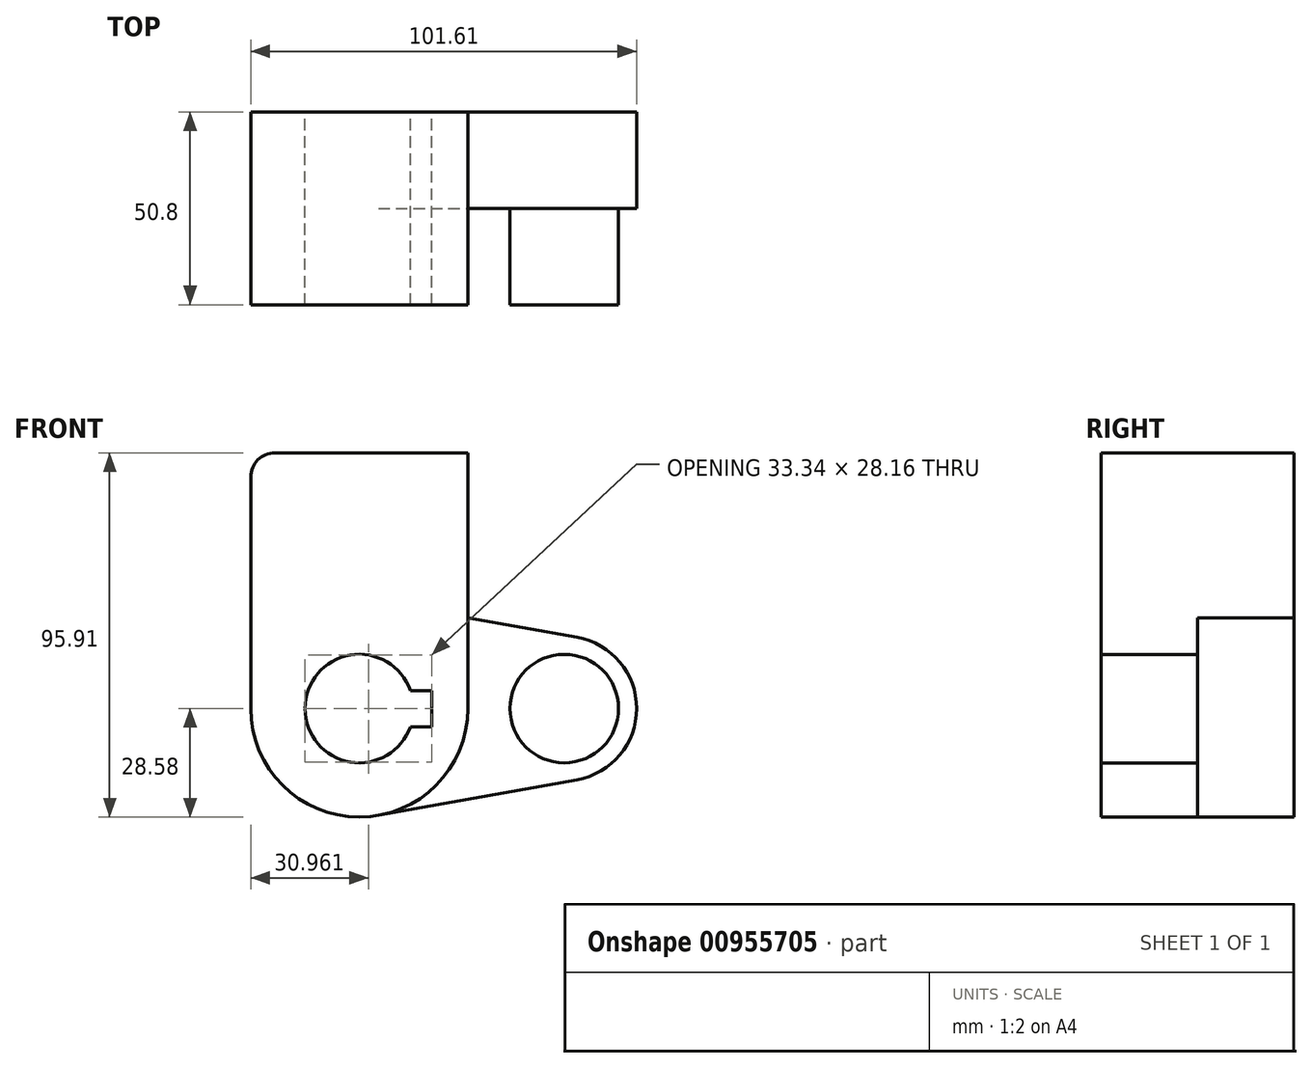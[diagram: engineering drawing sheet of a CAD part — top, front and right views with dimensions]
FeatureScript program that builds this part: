
annotation { "Feature Type Name" : "Feature", "Feature Type Description" : "" }
export const myFeature = defineFeature(function(context is Context, id is Id, definition is map)
    precondition{}
    {
        {
            var Q0;
            Q0=qCreatedBy(makeId("Front.planeOp"),FACE);
            var sketch = newSketch(context, id + "F0", { "sketchPlane" : qUnion([Q0])});
            skCircle(sketch, "E0", {"center": v(0, 0) * mm, "radius": 28.58 * mm});
            skCircle(sketch, "E1", {"center": v(53.98, 0) * mm, "radius": 19.05 * mm});
            skLineSegment(sketch, "E2", {"start": v(5.04, 28.13) * mm, "end": v(57.34, 18.75) * mm});
            skLineSegment(sketch, "E3", {"start": v(5.04, -28.13) * mm, "end": v(57.34, -18.75) * mm});
            skCircle(sketch, "E4", {"center": v(0, 0) * mm, "radius": 14.29 * mm});
            skCircle(sketch, "E5", {"center": v(53.98, 0) * mm, "radius": 14.29 * mm});
            skLineSegment(sketch, "E6.bottom", {"start": v(19.05, -4.76) * mm, "end": v(-19.05, -4.76) * mm});
            skLineSegment(sketch, "E6.top", {"start": v(19.05, 4.76) * mm, "end": v(-19.05, 4.76) * mm});
            skLineSegment(sketch, "E6.left", {"start": v(19.05, -4.76) * mm, "end": v(19.05, 4.76) * mm});
            skLineSegment(sketch, "E6.right", {"start": v(-19.05, -4.76) * mm, "end": v(-19.05, 4.76) * mm});
            skSolve(sketch);
        }
        {
            var Q0;
            {var subQ7=sQuery(id+"F0.wireOp",EDGE,"E6.left");Q0=makeQuery(id+"F0.imprint","IMPRINT",FACE,{"disambiguationData":[TD([[makeQuery(id+"F0.imprint","IMPRINT",EDGE,{"derivedFrom":subQ7}),-1.0]])]});}
            var Q1;
            {var subQ5=sQuery(id+"F0.wireOp",EDGE,"E6.right");Q1=makeQuery(id+"F0.imprint","IMPRINT",FACE,{"disambiguationData":[TD([[makeQuery(id+"F0.imprint","IMPRINT",EDGE,{"derivedFrom":subQ5}),-1.0]])]});}
            var Q2;
            {var subQ0=sQuery(id+"F0.wireOp",EDGE,"E2");Q2=makeQuery(id+"F0.imprint","IMPRINT",FACE,{"disambiguationData":[TD([[makeQuery(id+"F0.imprint","IMPRINT",EDGE,{"derivedFrom":subQ0}),-1.0]])]});}
            var Q3;
            Q3=makeQuery(id+"F0.imprint","IMPRINT",FACE,{"disambiguationData":[TD([[makeQuery(id+"F0.imprint","IMPRINT",EDGE,{"derivedFrom":sQuery(id+"F0.wireOp",EDGE,"E5")}),-1.0]])]});
            extrude(context, id + "F1", {"entities" : qUnion([Q0, Q1, Q2, Q3]), "depth" : 25.4 * mm, "offsetDistance" : 25.4 * mm});
        }
        {
            var Q0;
            {var subQ7=sQuery(id+"F0.wireOp",EDGE,"E6.left");Q0=makeQuery(id+"F0.imprint","IMPRINT",FACE,{"disambiguationData":[TD([[makeQuery(id+"F0.imprint","IMPRINT",EDGE,{"derivedFrom":subQ7}),-1.0]])]});}
            var Q1;
            {var subQ5=sQuery(id+"F0.wireOp",EDGE,"E6.right");Q1=makeQuery(id+"F0.imprint","IMPRINT",FACE,{"disambiguationData":[TD([[makeQuery(id+"F0.imprint","IMPRINT",EDGE,{"derivedFrom":subQ5}),-1.0]])]});}
            extrude(context, id + "F2", {"entities" : qUnion([Q0, Q1]), "operationType" : NewBodyOperationType.ADD, "depth" : 50.8 * mm, "offsetDistance" : 25.4 * mm});
        }
        {
            var Q0;
            Q0=makeQuery(id+"F2.opExtrude","CAP_FACE",FACE,{"disambiguationData":[OSD([sQuery(id+"F0.wireOp",EDGE,"E0"),sQuery(id+"F0.wireOp",EDGE,"E4"),sQuery(id+"F0.wireOp",EDGE,"E6.bottom"),sQuery(id+"F0.wireOp",EDGE,"E6.top"),sQuery(id+"F0.wireOp",EDGE,"E6.left")])],"isStart":false});
            var sketch = newSketch(context, id + "F3", { "sketchPlane" : qUnion([Q0])});
            skLineSegment(sketch, "E7", {"start": v(-28.58, 0) * mm, "end": v(-28.58, 60.98) * mm});
            skLineSegment(sketch, "E8", {"start": v(-22.23, 67.33) * mm, "end": v(28.57, 67.33) * mm});
            skLineSegment(sketch, "E9", {"start": v(28.58, 67.33) * mm, "end": v(28.58, 0) * mm});
            skLineSegment(sketch, "E10", {"start": v(-13.78, 67.33) * mm, "end": v(-13.78, 25.03) * mm, "construction": true});
            skLineSegment(sketch, "E11", {"start": v(3.87, 28.31) * mm, "end": v(3.87, 67.33) * mm, "construction": true});
            skPoint(sketch, "E12.visualSharp", {"position": v(-28.58, 67.33) * mm});
            skArc(sketch, "E12.filletArc", {"start": v(-22.23, 67.33) * mm, "mid": v(-26.72, 65.47) * mm, "end": v(-28.58, 60.98) * mm});
            skLineSegment(sketch, "E13.0", {"start": v(-22.23, 80.03) * mm, "end": v(28.57, 80.03) * mm});
            skArc(sketch, "E13.1", {"start": v(-22.23, 80.03) * mm, "mid": v(-35.7, 74.45) * mm, "end": v(-41.28, 60.98) * mm});
            skLineSegment(sketch, "E13.2", {"start": v(-41.27, 0) * mm, "end": v(-41.28, 60.98) * mm});
            skCircle(sketch, "E14.0", {"center": v(53.98, 0) * mm, "radius": 14.29 * mm});
            skSolve(sketch);
        }
        {
            var Q0;
            {var subQ1=sQuery(id+"F3.wireOp",EDGE,"E7");Q0=makeQuery(id+"F3.imprint","IMPRINT",FACE,{"disambiguationData":[TD([[makeQuery(id+"F3.imprint","IMPRINT",EDGE,{"derivedFrom":subQ1}),-1.0]])]});}
            var Q1;
            Q1=makeQuery(id+"F3.imprint","IMPRINT",FACE,{"disambiguationData":[TD([[makeQuery(id+"F3.imprint","IMPRINT",EDGE,{"derivedFrom":sQuery(id+"F3.wireOp",EDGE,"E14.0")}),1.0]])]});
            var Q2;
            Q2=makeQuery(id+"F1.opExtrude","CAP_FACE",FACE,{"disambiguationData":[OSD([sQuery(id+"F0.wireOp",EDGE,"E0"),sQuery(id+"F0.wireOp",EDGE,"E1"),sQuery(id+"F0.wireOp",EDGE,"E2"),sQuery(id+"F0.wireOp",EDGE,"E3"),sQuery(id+"F0.wireOp",EDGE,"E4"),sQuery(id+"F0.wireOp",EDGE,"E5"),sQuery(id+"F0.wireOp",EDGE,"E6.bottom"),sQuery(id+"F0.wireOp",EDGE,"E6.top"),sQuery(id+"F0.wireOp",EDGE,"E6.left")])],"isStart":true});
            extrude(context, id + "F4", {"entities" : qUnion([Q0, Q1]), "operationType" : NewBodyOperationType.ADD, "endBound" : BoundingType.UP_TO_SURFACE, "oppositeDirection" : true, "depth" : 25.4 * mm, "endBoundEntityFace" : qUnion([Q2]), "offsetDistance" : 25.4 * mm});
        }
    });
